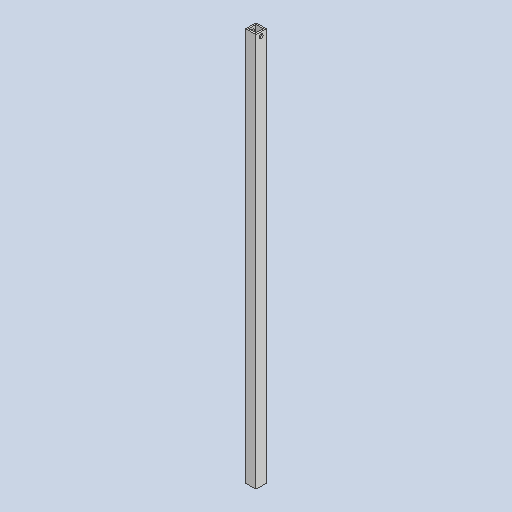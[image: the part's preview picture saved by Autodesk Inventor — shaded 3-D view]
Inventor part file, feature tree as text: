
AUTODESK INVENTOR PART (.ipt)
format: ipt  version: 2022 (Build 260153000, 153)  size: 122,368 bytes
history: native  units: in
note: dims shown in document units (in); Inventor stores cm internally (conversion verified against a paired STEP export)
features: extrude x3, sketch x3, other x3, reference x1
ambient origin geometry x8: Origin, YZ Plane, XZ Plane, XY Plane, X Axis, Y Axis, Z Axis, Center Point
bodies: Solid1 (feature_tree)
feature tree (10):
  extrude  "Extrusion1"  Depth=0.7874in
  extrude  "Extrusion2"  Depth=0.1181in
  extrude  "Extrusion3"  Depth=0.1181in
  sketch  "Sketch1"  dims[d0=0.7874in d1=0.7874in]
  sketch  "Sketch2"  dims[d2=0.1181in d3=0.1181in]
  sketch  "Sketch3"  dims[d4=0.1181in d5=0.1181in d6=30.1181in d7=0.0in d8=0.315in d9=0.315in d10=19.685in d11=0.0in d12=0.3937in d13=0.0in]
  reference  "Reference1"
  parser-record x1  (decoder bookkeeping rows leaked as tree rows — omitted from the tree; the rows remain in map.json)
  other  "model.iam"
  other  "enc holder:1"
note: 1 file-system path scrubbed to <path> (originals preserved in map.json)
